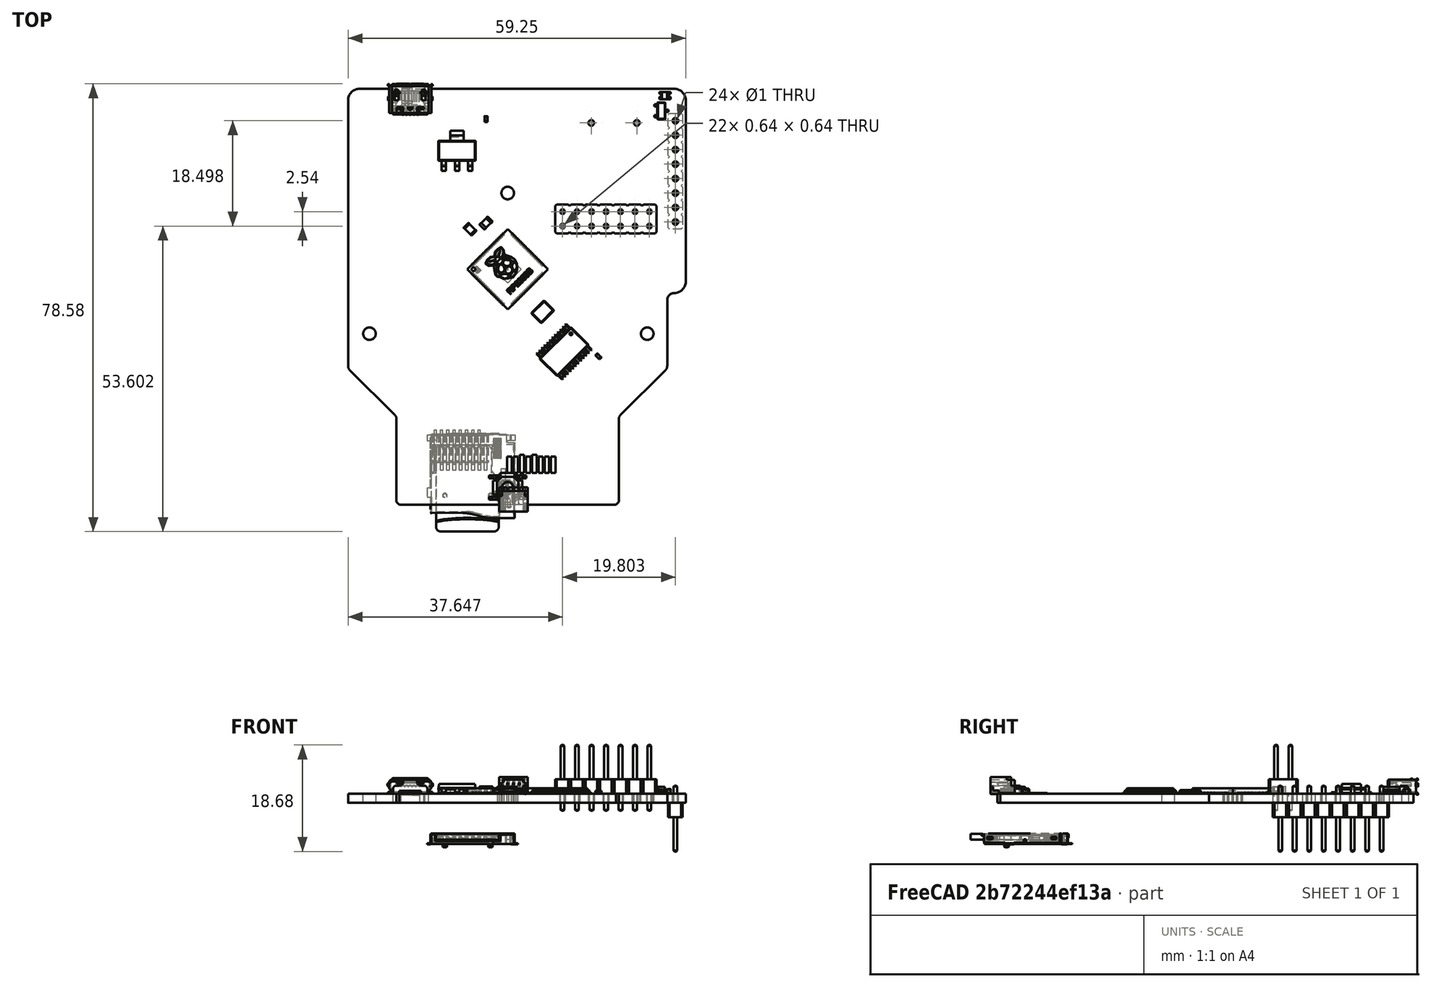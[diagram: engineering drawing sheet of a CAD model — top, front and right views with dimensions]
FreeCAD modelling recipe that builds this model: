
FCSTD DOCUMENT  (FreeCAD 1.0R39285 (Git))
Label: DecentCart2350Board
License: All rights reserved
LicenseURL: http://en.wikipedia.org/wiki/All_rights_reserved
objects: Part::Feature×97, App::Link×62, App::Part×27, PartDesign::CoordinateSystem×1, Sketcher::SketchObject×1
note: 100 computed .brp shape members not serialized (recipe doc carries the construction recipe); baked Part::Feature solids carry a one-line shape summary decoded from their .brp

FEATURE [PartDesign::CoordinateSystem] Local_CS_9dbe
  AttacherType = Attacher::AttachEngine3D
  MapMode = 2
FEATURE [Part::Feature] Pcb_9dbe
  Placement = pos=(-149.761,121.317,0) rot=(0,0,1;0rad)
  shape: bbox 59.25 x 73 x 1.6 mm, 71 faces (baked)
FEATURE [Sketcher::SketchObject] PCB_Sketch_9dbe
  ArcFitTolerance = 1e-06
  FullyConstrained = false
  MakeInternals = false
  sketch-geometry (19):
    g0: LineSegment StartX=19.7929 StartY=12.7071 StartZ=0 EndX=27.7071 EndY=20.6229 EndZ=0
    g1: LineSegment StartX=19.5 StartY=-2.5 StartZ=0 EndX=19.5 EndY=12 EndZ=0
    g2: LineSegment StartX=-26 StartY=70 StartZ=0 EndX=29.25 EndY=70 EndZ=0
    g3: LineSegment StartX=19 StartY=-3 StartZ=0 EndX=19.5 EndY=-2.5 EndZ=0
    g4: LineSegment StartX=28 StartY=32.89 StartZ=0 EndX=28 EndY=21.33 EndZ=0
    g5: LineSegment StartX=19 StartY=-3 StartZ=0 EndX=-19 EndY=-3 EndZ=0
    g6: LineSegment StartX=-28 StartY=21.3171 StartZ=0 EndX=-28 EndY=68 EndZ=0
    g7: LineSegment StartX=31.25 StartY=36.14 StartZ=0 EndX=31.25 EndY=68 EndZ=0
    g8: LineSegment StartX=-19.7929 StartY=12.7071 StartZ=0 EndX=-27.7071 EndY=20.61 EndZ=0
    g9: LineSegment StartX=-19 StartY=-3 StartZ=0 EndX=-19.5 EndY=-2.5 EndZ=0
    g10: LineSegment StartX=-19.5 StartY=-2.5 StartZ=0 EndX=-19.5 EndY=12 EndZ=0
    g11: ArcOfCircle CenterX=-20.5001 CenterY=12 CenterZ=0 NormalX=0 NormalY=0 NormalZ=-1 AngleXU=2.35623 Radius=1.00008 StartAngle=0 EndAngle=0.78533
    g12: ArcOfCircle CenterX=29.25 CenterY=36.14 CenterZ=0 NormalX=0 NormalY=0 NormalZ=-1 AngleXU=3.14159 Radius=2 StartAngle=0 EndAngle=1.5708
    g13: ArcOfCircle CenterX=29.25 CenterY=32.89 CenterZ=0 NormalX=0 NormalY=0 NormalZ=-1 AngleXU=1.30145e-06 Radius=1.25 StartAngle=0 EndAngle=1.57079
    g14: ArcOfCircle CenterX=20.5 CenterY=12 CenterZ=0 NormalX=0 NormalY=0 NormalZ=-1 AngleXU=1.0278e-05 Radius=1.00003 StartAngle=0 EndAngle=0.785377
    g15: ArcOfCircle CenterX=29.25 CenterY=68 CenterZ=0 NormalX=0 NormalY=0 NormalZ=-1 AngleXU=1.5708 Radius=2 StartAngle=0 EndAngle=1.5708
    g16: ArcOfCircle CenterX=-27 CenterY=21.3171 CenterZ=0 NormalX=0 NormalY=0 NormalZ=-1 AngleXU=-0.785398 Radius=0.999999 StartAngle=0 EndAngle=0.785399
    g17: ArcOfCircle CenterX=-26 CenterY=68 CenterZ=0 NormalX=0 NormalY=0 NormalZ=-1 AngleXU=-7.47076e-07 Radius=2 StartAngle=0 EndAngle=1.5708
    g18: ArcOfCircle CenterX=27 CenterY=21.33 CenterZ=0 NormalX=0 NormalY=0 NormalZ=-1 AngleXU=3.14158 Radius=0.999978 StartAngle=0 EndAngle=0.785416
  constraints (19):
    c: Coincident(g6,g16)
    c: Coincident(g6,g17)
    c: Coincident(g8,g16)
    c: Coincident(g2,g17)
    c: Coincident(g8,g11)
    c: Coincident(g9,g10)
    c: Coincident(g10,g11)
    c: Coincident(g5,g9)
    c: Coincident(g3,g5)
    c: Coincident(g1,g3)
    c: Coincident(g1,g14)
    c: Coincident(g0,g14)
    c: Coincident(g0,g18)
    c: Coincident(g4,g18)
    c: Coincident(g4,g13)
    c: Coincident(g12,g13)
    c: Coincident(g2,g15)
    c: Coincident(g7,g12)
    c: Coincident(g7,g15)
FEATURE [App::Part] Board_Geoms_9dbe
  Group = -> [Pcb_9dbe,PCB_Sketch_9dbe]
  Origin = -> Origin
FEATURE [Part::Feature] Shape  label="U6_TSSOP_24_44x78mm_P065mm_249428eb97b7"
  Placement = pos=(9.906,23.836,0) rot=(0,0,-1;0.785398rad)
  shape: bbox 9.765 x 9.765 x 0.97 mm, 396 faces (baked)
FEATURE [Part::Feature] Shape001  label="R30_R_0402_1005Metric_56d1e8ac7ec3"
  Placement = pos=(-3.7846,64.6938,0) rot=(0,0,1;1.5708rad)
  shape: bbox 0.5 x 1 x 0.35 mm, 26 faces (baked)
FEATURE [Part::Feature] Shape002  label="C33_C_0402_1005Metric_439f5c97a156"
  Placement = pos=(15.9258,23.0232,0) rot=(0,0,1;2.35619rad)
  shape: bbox 1.061 x 1.061 x 0.5 mm, 28 faces (baked)
FEATURE [Part::Feature] Shape003  label="U3_RP2350B_5bf34b71a8d2"
  Placement = pos=(0,38.314,0) rot=(0,0,1;0.785398rad)
  shape: bbox 14.16 x 14.16 x 0.9762 mm, 744 faces (baked)
FEATURE [App::Link] C33_C_0402_1005Metric_439f5c97a156_ln_  label="C29_C_0402_1005Metric_d980d0f3218c"
  LinkPlacement = pos=(4.8514,21.55,0) rot=(0,0,1;3.14159rad)
  LinkedObject = -> Shape002
  Placement = pos=(4.8514,21.55,0) rot=(0,0,1;3.14159rad)
FEATURE [App::Link] C33_C_0402_1005Metric_439f5c97a156_ln_001  label="C10_C_0402_1005Metric_251042c45dc4"
  LinkPlacement = pos=(4.9784,42.5812,0) rot=(0,0,1;0.785398rad)
  LinkedObject = -> Shape002
  Placement = pos=(4.9784,42.5812,0) rot=(0,0,1;0.785398rad)
FEATURE [App::Link] R30_R_0402_1005Metric_56d1e8ac7ec3_ln_  label="R10_R_0402_1005Metric_51b1b8e8657a"
  LinkPlacement = pos=(-11.1506,31.4306,0) rot=(0,0,1;3.92699rad)
  LinkedObject = -> Shape001
  Placement = pos=(-11.1506,31.4306,0) rot=(0,0,1;3.92699rad)
FEATURE [App::Link] R30_R_0402_1005Metric_56d1e8ac7ec3_ln_001  label="R24_R_0402_1005Metric_4880820e7255"
  LinkPlacement = pos=(5.7404,41.8338,0) rot=(0,0,1;0.785398rad)
  LinkedObject = -> Shape001
  Placement = pos=(5.7404,41.8338,0) rot=(0,0,1;0.785398rad)
FEATURE [App::Link] C33_C_0402_1005Metric_439f5c97a156_ln_002  label="C39_C_0402_1005Metric_aed9d11787dd"
  LinkPlacement = pos=(21.4376,27.9508,0) rot=(0,0,1;0.785398rad)
  LinkedObject = -> Shape002
  Placement = pos=(21.4376,27.9508,0) rot=(0,0,1;0.785398rad)
FEATURE [App::Link] R30_R_0402_1005Metric_56d1e8ac7ec3_ln_002  label="R7_R_0402_1005Metric_6c02ad4cb323"
  LinkPlacement = pos=(20.32,51.1302,0) rot=(0,0,1;1.5708rad)
  LinkedObject = -> Shape001
  Placement = pos=(20.32,51.1302,0) rot=(0,0,1;1.5708rad)
FEATURE [App::Link] R30_R_0402_1005Metric_56d1e8ac7ec3_ln_003  label="R6_R_0402_1005Metric_24b84eea597d"
  LinkPlacement = pos=(17.4752,51.1302,0) rot=(0,0,1;1.5708rad)
  LinkedObject = -> Shape001
  Placement = pos=(17.4752,51.1302,0) rot=(0,0,1;1.5708rad)
FEATURE [App::Link] C33_C_0402_1005Metric_439f5c97a156_ln_003  label="C24_C_0402_1005Metric_bb1ce9836f4d"
  LinkPlacement = pos=(4.3434,28.9922,0) rot=(0,0,1;2.35619rad)
  LinkedObject = -> Shape002
  Placement = pos=(4.3434,28.9922,0) rot=(0,0,1;2.35619rad)
FEATURE [App::Link] U6_TSSOP_24_44x78mm_P065mm_249428eb97b7_ln_  label="U5_TSSOP_24_44x78mm_P065mm_d589b01f07bd"
  LinkPlacement = pos=(-0.254,19.518,0) rot=(0,0,-1;1.5708rad)
  LinkedObject = -> Shape
  Placement = pos=(-0.254,19.518,0) rot=(0,0,-1;1.5708rad)
FEATURE [Part::Feature] Shape004  label="R28_R_0805_2012Metric_252277e7415b"
  Placement = pos=(-6.604,45.339,0) rot=(0,0,-1;0.785398rad)
  shape: bbox 2.263 x 2.263 x 0.45 mm, 26 faces (baked)
FEATURE [App::Link] R30_R_0402_1005Metric_56d1e8ac7ec3_ln_004  label="R9_R_0402_1005Metric_bd238e743bb6"
  LinkPlacement = pos=(23.1648,51.1302,0) rot=(0,0,1;1.5708rad)
  LinkedObject = -> Shape001
  Placement = pos=(23.1648,51.1302,0) rot=(0,0,1;1.5708rad)
FEATURE [App::Link] C33_C_0402_1005Metric_439f5c97a156_ln_004  label="C16_C_0402_1005Metric_04ddee7b3d28"
  LinkPlacement = pos=(19.3802,51.1556,0) rot=(0,0,1;1.5708rad)
  LinkedObject = -> Shape002
  Placement = pos=(19.3802,51.1556,0) rot=(0,0,1;1.5708rad)
FEATURE [App::Link] C33_C_0402_1005Metric_439f5c97a156_ln_005  label="C25_C_0402_1005Metric_b25ebf576064"
  LinkPlacement = pos=(4.3942,32.1926,0) rot=(0,0,1;0.785398rad)
  LinkedObject = -> Shape002
  Placement = pos=(4.3942,32.1926,0) rot=(0,0,1;0.785398rad)
FEATURE [Part::Feature] Part__Feature  label="TS-1187A v2"
  shape: bbox 5.1 x 5.1 x 1.2 mm, 48 faces (baked)
FEATURE [Part::Feature] Part__Feature001  label="TS-1187A v003"
  shape: bbox 2 x 2 x 1.4 mm, 4 faces (baked)
FEATURE [Part::Feature] Part__Feature002  label="TS-1187A v004"
  shape: bbox 1.15 x 1.15 x 0.7 mm, 10 faces (baked)
FEATURE [Part::Feature] Part__Feature003  label="TS-1187A v005"
  shape: bbox 1.15 x 1.15 x 0.7 mm, 10 faces (baked)
FEATURE [Part::Feature] Part__Feature004  label="TS-1187A v006"
  shape: bbox 1.15 x 1.15 x 0.7 mm, 10 faces (baked)
FEATURE [Part::Feature] Part__Feature005  label="TS-1187A v007"
  shape: bbox 1.15 x 1.15 x 0.7 mm, 10 faces (baked)
FEATURE [Part::Feature] Part__Feature006  label="TS-1187A v008"
  shape: bbox 1.55 x 0.5 x 0.2 mm, 10 faces (baked)
FEATURE [Part::Feature] Part__Feature007  label="TS-1187A v009"
  shape: bbox 1.55 x 0.5 x 0.2 mm, 10 faces (baked)
FEATURE [Part::Feature] Part__Feature008  label="TS-1187A v010"
  shape: bbox 1.55 x 0.5 x 0.2 mm, 10 faces (baked)
FEATURE [Part::Feature] Part__Feature009  label="TS-1187A v011"
  shape: bbox 1.55 x 0.5 x 0.2 mm, 10 faces (baked)
FEATURE [App::Part] TS_1187A_v2  label="SW3_TS-1187A v012_8148cfb37216"
  Group = -> [Part__Feature,Part__Feature001,Part__Feature002,Part__Feature003,Part__Feature004,Part__Feature005,Part__Feature006,Part__Feature007,Part__Feature008,Part__Feature009]
  Origin = -> Origin008
  Placement = pos=(4.5,67.1,0) rot=(0,0,1;3.14159rad)
FEATURE [App::Link] R30_R_0402_1005Metric_56d1e8ac7ec3_ln_005  label="R36_R_0402_1005Metric_a48c821af01a"
  LinkPlacement = pos=(-17.52,43.93,0) rot=(0,0,1;0.785398rad)
  LinkedObject = -> Shape001
  Placement = pos=(-17.52,43.93,0) rot=(0,0,1;0.785398rad)
FEATURE [App::Link] U6_TSSOP_24_44x78mm_P065mm_249428eb97b7_ln_001  label="U1_TSSOP_24_44x78mm_P065mm_cca0021ee69b"
  LinkPlacement = pos=(-16.51,29.932,0) rot=(0,0,1;3.92699rad)
  LinkedObject = -> Shape
  Placement = pos=(-16.51,29.932,0) rot=(0,0,1;3.92699rad)
FEATURE [App::Link] R30_R_0402_1005Metric_56d1e8ac7ec3_ln_006  label="R8_R_0402_1005Metric_3dfb7eb72526"
  LinkPlacement = pos=(22.098,51.1302,0) rot=(0,0,1;1.5708rad)
  LinkedObject = -> Shape001
  Placement = pos=(22.098,51.1302,0) rot=(0,0,1;1.5708rad)
FEATURE [Part::Feature] Part__Feature010  label="Contact009"
  Placement = pos=(-13.13,0,0) rot=(0,0,1;0rad)
  shape: bbox 0.9 x 1.8 x 0.4546 mm, 22 faces (baked)
FEATURE [Part::Feature] Part__Feature011  label="Contact008"
  Placement = pos=(-7.7,0,0) rot=(0,0,1;0rad)
  shape: bbox 0.9 x 6.04 x 0.9096 mm, 26 faces (baked)
FEATURE [Part::Feature] Part__Feature012  label="Contact007"
  Placement = pos=(-6.6,0,0) rot=(0,0,1;0rad)
  shape: bbox 0.9 x 6.04 x 0.9096 mm, 26 faces (baked)
FEATURE [Part::Feature] Part__Feature013  label="Contact006"
  Placement = pos=(-5.5,0,0) rot=(0,0,1;0rad)
  shape: bbox 0.9 x 6.04 x 0.9096 mm, 26 faces (baked)
FEATURE [Part::Feature] Part__Feature014  label="Contact005"
  Placement = pos=(-4.4,0,0) rot=(0,0,1;0rad)
  shape: bbox 0.9 x 6.04 x 0.9096 mm, 26 faces (baked)
FEATURE [Part::Feature] Part__Feature015  label="Contact004"
  Placement = pos=(-3.3,0,0) rot=(0,0,1;0rad)
  shape: bbox 0.9 x 6.04 x 0.9096 mm, 26 faces (baked)
FEATURE [Part::Feature] Part__Feature016  label="Contact003"
  Placement = pos=(-2.2,0,0) rot=(0,0,1;0rad)
  shape: bbox 0.9 x 6.04 x 0.9096 mm, 26 faces (baked)
FEATURE [Part::Feature] Part__Feature017  label="Contact002"
  Placement = pos=(-1.1,0,0) rot=(0,0,1;0rad)
  shape: bbox 0.9 x 6.04 x 0.9096 mm, 26 faces (baked)
FEATURE [App::Part] cont
  Group = -> [Part__Feature010,Part__Feature011,Part__Feature012,Part__Feature013,Part__Feature014,Part__Feature015,Part__Feature016,Part__Feature017]
  Origin = -> Origin009
FEATURE [Part::Feature] Part__Feature018  label="frame002"
  Placement = pos=(0.05,0,-8.83) rot=(0,0,1;0rad)
  shape: bbox 14.8 x 14.69 x 2.22 mm, 238 faces (baked)
FEATURE [Part::Feature] Part__Feature019  label="cover001"
  Placement = pos=(0.3,1.14,-0.54) rot=(0.706791,-0.029864,0.706791;3.07998rad)
  shape: bbox 15.98 x 14.86 x 1.92 mm, 162 faces (baked)
FEATURE [Part::Feature] Part__Feature020  label="spring"
  Placement = pos=(-1.82,8.5,-8.08) rot=(0.15487,0.698575,-0.698575;2.83429rad)
  shape: bbox 1.439 x 3.68 x 1.439 mm, 10 faces (baked)
FEATURE [App::Part] microSD_card_slot  label="J1_microSD_card_slot_e46293b91a5e"
  Group = -> [cont,Part__Feature018,Part__Feature019,Part__Feature020]
  Origin = -> Origin010
  Placement = pos=(11.59,62.758,8.9) rot=(0,0,1;3.14159rad)
FEATURE [Part::Feature] Part__Feature021  label="cont002"
  Placement = pos=(6.9,4,0) rot=(0,0,1;0rad)
  shape: bbox 0.8 x 2.9 x 0.1 mm, 6 faces (baked)
FEATURE [Part::Feature] Part__Feature022  label="cont003"
  Placement = pos=(5.8,4,0) rot=(0,0,1;0rad)
  shape: bbox 0.8 x 2.9 x 0.1 mm, 6 faces (baked)
FEATURE [Part::Feature] Part__Feature023  label="cont005"
  Placement = pos=(3.6,4,0) rot=(0,0,1;0rad)
  shape: bbox 0.8 x 2.9 x 0.1 mm, 6 faces (baked)
FEATURE [Part::Feature] Part__Feature024  label="cont006"
  Placement = pos=(2.5,4.15,0) rot=(0,0,1;0rad)
  shape: bbox 0.8 x 3.2 x 0.1 mm, 6 faces (baked)
FEATURE [Part::Feature] Part__Feature025  label="cont007"
  Placement = pos=(1.4,4,0) rot=(0,0,1;0rad)
  shape: bbox 0.8 x 2.9 x 0.1 mm, 6 faces (baked)
FEATURE [Part::Feature] Part__Feature026  label="cont008"
  Placement = pos=(0.3,4,0) rot=(0,0,1;0rad)
  shape: bbox 0.8 x 2.9 x 0.1 mm, 6 faces (baked)
FEATURE [Part::Feature] Part__Feature027  label="cont001"
  Placement = pos=(8,4,0) rot=(0,0,1;0rad)
  shape: bbox 0.8 x 2.9 x 0.1 mm, 6 faces (baked)
FEATURE [Part::Feature] Part__Feature028  label="cont004"
  Placement = pos=(4.7,4.15,0) rot=(0,0,1;0rad)
  shape: bbox 0.8 x 3.2 x 0.1 mm, 6 faces (baked)
FEATURE [App::Part] contacts
  Group = -> [Part__Feature021,Part__Feature022,Part__Feature023,Part__Feature024,Part__Feature025,Part__Feature026,Part__Feature027,Part__Feature028]
  Origin = -> Origin011
  Placement = pos=(-11.8,0.74,-8.1) rot=(0,0,1;0rad)
FEATURE [Part::Feature] Part__Feature029  label="body"
  Placement = pos=(-7.65,2.35,-8.04) rot=(0,0,1;0rad)
  shape: bbox 11.09 x 15 x 1 mm, 19 faces (baked)
FEATURE [Part::Feature] Part__Feature030  label="microSD001"
  Placement = pos=(-9.65,-4.1,-7.33) rot=(0,0,1;0rad)
  shape: bbox 1.052 x 0.727 x 2e-07 mm, 1 faces, 0 solids (baked)
FEATURE [Part::Feature] Part__Feature031  label="microSD002"
  Placement = pos=(-9.65,-4.1,-7.33) rot=(0,0,1;0rad)
  shape: bbox 0.1517 x 0.7132 x 2e-07 mm, 1 faces, 0 solids (baked)
FEATURE [Part::Feature] Part__Feature032  label="microSD003"
  Placement = pos=(-9.65,-4.1,-7.33) rot=(0,0,1;0rad)
  shape: bbox 0.1704 x 0.168 x 2e-07 mm, 1 faces, 0 solids (baked)
FEATURE [Part::Feature] Part__Feature033  label="microSD004"
  Placement = pos=(-9.65,-4.1,-7.33) rot=(0,0,1;0rad)
  shape: bbox 0.546 x 0.7407 x 2e-07 mm, 1 faces, 0 solids (baked)
FEATURE [Part::Feature] Part__Feature034  label="microSD005"
  Placement = pos=(-9.65,-4.1,-7.33) rot=(0,0,1;0rad)
  shape: bbox 0.4376 x 0.727 x 2e-07 mm, 1 faces, 0 solids (baked)
FEATURE [Part::Feature] Part__Feature035  label="microSD006"
  Placement = pos=(-9.65,-4.1,-7.33) rot=(0,0,1;0rad)
  shape: bbox 0.6757 x 0.7407 x 2e-07 mm, 1 faces, 0 solids (baked)
FEATURE [Part::Feature] Part__Feature036  label="microSD007"
  Placement = pos=(-9.65,-4.1,-7.33) rot=(0,0,1;0rad)
  shape: bbox 0.6041 x 0.972 x 2e-07 mm, 1 faces, 0 solids (baked)
FEATURE [Part::Feature] Part__Feature037  label="microSD008"
  Placement = pos=(-9.65,-4.1,-7.33) rot=(0,0,1;0rad)
  shape: bbox 0.7674 x 0.9445 x 2e-07 mm, 1 faces, 0 solids (baked)
FEATURE [App::Part] microSD009
  Group = -> [Part__Feature030,Part__Feature031,Part__Feature032,Part__Feature033,Part__Feature034,Part__Feature035,Part__Feature036,Part__Feature037]
  Origin = -> Origin012
FEATURE [Part::Feature] Part__Feature038  label="DATA2"
  Placement = pos=(-4.04,1.23,-8.06) rot=(0.707107,0.707107,0;3.14159rad)
  shape: bbox 0.4723 x 0.3582 x 2e-07 mm, 1 faces, 0 solids (baked)
FEATURE [Part::Feature] Part__Feature039  label="DATA003"
  Placement = pos=(-4.04,1.23,-8.06) rot=(0.707107,0.707107,0;3.14159rad)
  shape: bbox 0.4736 x 0.3966 x 2e-07 mm, 1 faces, 0 solids (baked)
FEATURE [Part::Feature] Part__Feature040  label="DATA004"
  Placement = pos=(-4.04,1.23,-8.06) rot=(0.707107,0.707107,0;3.14159rad)
  shape: bbox 0.4723 x 0.3398 x 2e-07 mm, 1 faces, 0 solids (baked)
FEATURE [Part::Feature] Part__Feature041  label="DATA005"
  Placement = pos=(-4.04,1.23,-8.06) rot=(0.707107,0.707107,0;3.14159rad)
  shape: bbox 0.4736 x 0.3966 x 2e-07 mm, 1 faces, 0 solids (baked)
FEATURE [Part::Feature] Part__Feature042  label="DATA006"
  Placement = pos=(-4.04,1.23,-8.06) rot=(0.707107,0.707107,0;3.14159rad)
  shape: bbox 0.4791 x 0.2953 x 2e-07 mm, 1 faces, 0 solids (baked)
FEATURE [App::Part] DATA007
  Group = -> [Part__Feature038,Part__Feature039,Part__Feature040,Part__Feature041,Part__Feature042]
  Origin = -> Origin013
FEATURE [Part::Feature] Part__Feature043  label="DATA3"
  Placement = pos=(-5.14,0.1,-8.06) rot=(0.707107,0.707107,0;3.14159rad)
  shape: bbox 0.4723 x 0.3582 x 2e-07 mm, 1 faces, 0 solids (baked)
FEATURE [Part::Feature] Part__Feature044  label="DATA008"
  Placement = pos=(-5.14,0.1,-8.06) rot=(0.707107,0.707107,0;3.14159rad)
  shape: bbox 0.4736 x 0.3966 x 2e-07 mm, 1 faces, 0 solids (baked)
FEATURE [Part::Feature] Part__Feature045  label="DATA009"
  Placement = pos=(-5.14,0.1,-8.06) rot=(0.707107,0.707107,0;3.14159rad)
  shape: bbox 0.4723 x 0.3398 x 2e-07 mm, 1 faces, 0 solids (baked)
FEATURE [Part::Feature] Part__Feature046  label="DATA010"
  Placement = pos=(-5.14,0.1,-8.06) rot=(0.707107,0.707107,0;3.14159rad)
  shape: bbox 0.4736 x 0.3966 x 2e-07 mm, 1 faces, 0 solids (baked)
FEATURE [Part::Feature] Part__Feature047  label="DATA011"
  Placement = pos=(-5.14,0.1,-8.06) rot=(0.707107,0.707107,0;3.14159rad)
  shape: bbox 0.486 x 0.3001 x 2e-07 mm, 1 faces, 0 solids (baked)
FEATURE [Part::Feature] Part__Feature048  label="DATA012"
  Placement = pos=(-5.14,0.1,-8.06) rot=(0.707107,0.707107,0;3.14159rad)
  shape: bbox 0.4723 x 0.2094 x 2e-07 mm, 1 faces, 0 solids (baked)
FEATURE [Part::Feature] Part__Feature049  label="DATA013"
  Placement = pos=(-5.14,0.1,-8.06) rot=(0.707107,0.707107,0;3.14159rad)
  shape: bbox 0.486 x 0.3482 x 2e-07 mm, 1 faces, 0 solids (baked)
FEATURE [Part::Feature] Part__Feature050  label="DATA014"
  Placement = pos=(-5.14,0.1,-8.06) rot=(0.707107,0.707107,0;3.14159rad)
  shape: bbox 0.4723 x 0.3582 x 2e-07 mm, 1 faces, 0 solids (baked)
FEATURE [App::Part] DATA015
  Group = -> [Part__Feature043,Part__Feature044,Part__Feature045,Part__Feature046,Part__Feature047,Part__Feature048,Part__Feature049,Part__Feature050]
  Origin = -> Origin014
FEATURE [Part::Feature] Part__Feature051  label="CMD"
  Placement = pos=(-6.23,1.68,-8.06) rot=(0.707107,0.707107,0;3.14159rad)
  shape: bbox 0.486 x 0.3482 x 2e-07 mm, 1 faces, 0 solids (baked)
FEATURE [Part::Feature] Part__Feature052  label="CMD001"
  Placement = pos=(-6.23,1.68,-8.06) rot=(0.707107,0.707107,0;3.14159rad)
  shape: bbox 0.4723 x 0.4369 x 2e-07 mm, 1 faces, 0 solids (baked)
FEATURE [Part::Feature] Part__Feature053  label="CMD002"
  Placement = pos=(-6.23,1.68,-8.06) rot=(0.707107,0.707107,0;3.14159rad)
  shape: bbox 0.4723 x 0.3582 x 2e-07 mm, 1 faces, 0 solids (baked)
FEATURE [App::Part] CMD003
  Group = -> [Part__Feature051,Part__Feature052,Part__Feature053]
  Origin = -> Origin015
FEATURE [Part::Feature] Part__Feature054  label="VDD"
  Placement = pos=(-7.32,1.83,-8.06) rot=(0.707107,0.707107,0;3.14159rad)
  shape: bbox 0.4723 x 0.3814 x 2e-07 mm, 1 faces, 0 solids (baked)
FEATURE [Part::Feature] Part__Feature055  label="VDD001"
  Placement = pos=(-7.32,1.83,-8.06) rot=(0.707107,0.707107,0;3.14159rad)
  shape: bbox 0.4723 x 0.3582 x 2e-07 mm, 1 faces, 0 solids (baked)
FEATURE [Part::Feature] Part__Feature056  label="VDD002"
  Placement = pos=(-7.32,1.83,-8.06) rot=(0.707107,0.707107,0;3.14159rad)
  shape: bbox 0.4723 x 0.3582 x 2e-07 mm, 1 faces, 0 solids (baked)
FEATURE [App::Part] VDD003
  Group = -> [Part__Feature054,Part__Feature055,Part__Feature056]
  Origin = -> Origin016
FEATURE [Part::Feature] Part__Feature057  label="CLK"
  Placement = pos=(-8.41,1.93,-8.06) rot=(0.707107,0.707107,0;3.14159rad)
  shape: bbox 0.486 x 0.3482 x 2e-07 mm, 1 faces, 0 solids (baked)
FEATURE [Part::Feature] Part__Feature058  label="CLK001"
  Placement = pos=(-8.41,1.93,-8.06) rot=(0.707107,0.707107,0;3.14159rad)
  shape: bbox 0.4723 x 0.2578 x 2e-07 mm, 1 faces, 0 solids (baked)
FEATURE [Part::Feature] Part__Feature059  label="CLK002"
  Placement = pos=(-8.41,1.93,-8.06) rot=(0.707107,0.707107,0;3.14159rad)
  shape: bbox 0.4723 x 0.3172 x 2e-07 mm, 1 faces, 0 solids (baked)
FEATURE [App::Part] CLK003
  Group = -> [Part__Feature057,Part__Feature058,Part__Feature059]
  Origin = -> Origin017
FEATURE [Part::Feature] Part__Feature060  label="GND"
  Placement = pos=(-9.5,1.68,-8.06) rot=(0.707107,0.707107,0;3.14159rad)
  shape: bbox 0.486 x 0.3847 x 2e-07 mm, 1 faces, 0 solids (baked)
FEATURE [Part::Feature] Part__Feature061  label="GND001"
  Placement = pos=(-9.5,1.68,-8.06) rot=(0.707107,0.707107,0;3.14159rad)
  shape: bbox 0.4723 x 0.343 x 2e-07 mm, 1 faces, 0 solids (baked)
FEATURE [Part::Feature] Part__Feature062  label="GND002"
  Placement = pos=(-9.5,1.68,-8.06) rot=(0.707107,0.707107,0;3.14159rad)
  shape: bbox 0.4723 x 0.3582 x 2e-07 mm, 1 faces, 0 solids (baked)
FEATURE [App::Part] GND003
  Group = -> [Part__Feature060,Part__Feature061,Part__Feature062]
  Origin = -> Origin018
FEATURE [Part::Feature] Part__Feature063  label="DATA0"
  Placement = pos=(-10.65,1.22,-8.06) rot=(0.707107,0.707107,0;3.14159rad)
  shape: bbox 0.4723 x 0.3582 x 2e-07 mm, 1 faces, 0 solids (baked)
FEATURE [Part::Feature] Part__Feature064  label="DATA016"
  Placement = pos=(-10.65,1.22,-8.06) rot=(0.707107,0.707107,0;3.14159rad)
  shape: bbox 0.4736 x 0.3966 x 2e-07 mm, 1 faces, 0 solids (baked)
FEATURE [Part::Feature] Part__Feature065  label="DATA017"
  Placement = pos=(-10.65,1.22,-8.06) rot=(0.707107,0.707107,0;3.14159rad)
  shape: bbox 0.4723 x 0.3398 x 2e-07 mm, 1 faces, 0 solids (baked)
FEATURE [Part::Feature] Part__Feature066  label="DATA018"
  Placement = pos=(-10.65,1.22,-8.06) rot=(0.707107,0.707107,0;3.14159rad)
  shape: bbox 0.4736 x 0.3966 x 2e-07 mm, 1 faces, 0 solids (baked)
FEATURE [Part::Feature] Part__Feature067  label="DATA019"
  Placement = pos=(-10.65,1.22,-8.06) rot=(0.707107,0.707107,0;3.14159rad)
  shape: bbox 0.486 x 0.3033 x 2e-07 mm, 1 faces, 0 solids (baked)
FEATURE [App::Part] DATA020
  Group = -> [Part__Feature063,Part__Feature064,Part__Feature065,Part__Feature066,Part__Feature067]
  Origin = -> Origin019
FEATURE [Part::Feature] Part__Feature068  label="DATA1"
  Placement = pos=(-11.75,1.26,-8.06) rot=(0.707107,0.707107,0;3.14159rad)
  shape: bbox 0.4723 x 0.3582 x 2e-07 mm, 1 faces, 0 solids (baked)
FEATURE [Part::Feature] Part__Feature069  label="DATA021"
  Placement = pos=(-11.75,1.26,-8.06) rot=(0.707107,0.707107,0;3.14159rad)
  shape: bbox 0.4736 x 0.3966 x 2e-07 mm, 1 faces, 0 solids (baked)
FEATURE [Part::Feature] Part__Feature070  label="DATA022"
  Placement = pos=(-11.75,1.26,-8.06) rot=(0.707107,0.707107,0;3.14159rad)
  shape: bbox 0.4723 x 0.3398 x 2e-07 mm, 1 faces, 0 solids (baked)
FEATURE [Part::Feature] Part__Feature071  label="DATA023"
  Placement = pos=(-11.75,1.26,-8.06) rot=(0.707107,0.707107,0;3.14159rad)
  shape: bbox 0.4736 x 0.3966 x 2e-07 mm, 1 faces, 0 solids (baked)
FEATURE [Part::Feature] Part__Feature072  label="DATA024"
  Placement = pos=(-11.75,1.26,-8.06) rot=(0.707107,0.707107,0;3.14159rad)
  shape: bbox 0.4723 x 0.1559 x 2e-07 mm, 1 faces, 0 solids (baked)
FEATURE [App::Part] DATA025
  Group = -> [Part__Feature068,Part__Feature069,Part__Feature070,Part__Feature071,Part__Feature072]
  Origin = -> Origin020
FEATURE [App::Part] sillk
  Group = -> [microSD009,DATA007,DATA015,CMD003,VDD003,CLK003,GND003,DATA020,DATA025]
  Origin = -> Origin021
FEATURE [App::Part] microSD  label="J1_microSD_e46293b91a5e[2]"
  Group = -> [contacts,Part__Feature029,sillk]
  Origin = -> Origin022
  Placement = pos=(11.52,64.008,8.8) rot=(0,0,1;3.14159rad)
FEATURE [App::Link] C33_C_0402_1005Metric_439f5c97a156_ln_006  label="C17_C_0402_1005Metric_c6ca86716594"
  LinkPlacement = pos=(-10.4902,30.7448,0) rot=(0,0,1;3.92699rad)
  LinkedObject = -> Shape002
  Placement = pos=(-10.4902,30.7448,0) rot=(0,0,1;3.92699rad)
FEATURE [App::Link] R30_R_0402_1005Metric_56d1e8ac7ec3_ln_007  label="R3_R_0402_1005Metric_55c9ecff9d97"
  LinkPlacement = pos=(-5.1054,25.36,0) rot=(0,0,1;3.92699rad)
  LinkedObject = -> Shape001
  Placement = pos=(-5.1054,25.36,0) rot=(0,0,1;3.92699rad)
FEATURE [App::Link] C33_C_0402_1005Metric_439f5c97a156_ln_007  label="C19_C_0402_1005Metric_aa6b38768ae2"
  LinkPlacement = pos=(-17.9832,24.5726,0) rot=(0,0,1;0.785398rad)
  LinkedObject = -> Shape002
  Placement = pos=(-17.9832,24.5726,0) rot=(0,0,1;0.785398rad)
FEATURE [App::Link] C33_C_0402_1005Metric_439f5c97a156_ln_008  label="C13_C_0402_1005Metric_ac4835eec644"
  LinkPlacement = pos=(-3.429,32.2688,0) rot=(0,0,1;3.92699rad)
  LinkedObject = -> Shape002
  Placement = pos=(-3.429,32.2688,0) rot=(0,0,1;3.92699rad)
FEATURE [App::Link] C33_C_0402_1005Metric_439f5c97a156_ln_009  label="C2_C_0402_1005Metric_d5aa21b2d2a1"
  LinkPlacement = pos=(-11.2268,17.8162,0) rot=(0,0,1;0.785398rad)
  LinkedObject = -> Shape002
  Placement = pos=(-11.2268,17.8162,0) rot=(0,0,1;0.785398rad)
FEATURE [App::Link] C33_C_0402_1005Metric_439f5c97a156_ln_010  label="C42_C_0402_1005Metric_3308e26e4d18"
  LinkPlacement = pos=(-12.44,51.24,0) rot=(0,0,1;3.92699rad)
  LinkedObject = -> Shape002
  Placement = pos=(-12.44,51.24,0) rot=(0,0,1;3.92699rad)
FEATURE [App::Link] C33_C_0402_1005Metric_439f5c97a156_ln_011  label="C21_C_0402_1005Metric_6886174ada46"
  LinkPlacement = pos=(-2.12,44.7,0) rot=(0,0,1;0.785398rad)
  LinkedObject = -> Shape002
  Placement = pos=(-2.12,44.7,0) rot=(0,0,1;0.785398rad)
FEATURE [App::Link] R30_R_0402_1005Metric_56d1e8ac7ec3_ln_008  label="R4_R_0402_1005Metric_b9c112d264e7"
  LinkPlacement = pos=(15.4432,51.1302,0) rot=(0,0,1;1.5708rad)
  LinkedObject = -> Shape001
  Placement = pos=(15.4432,51.1302,0) rot=(0,0,1;1.5708rad)
FEATURE [App::Link] C33_C_0402_1005Metric_439f5c97a156_ln_012  label="C6_C_0402_1005Metric_b7d84032a39b"
  LinkPlacement = pos=(-4.8768,33.7166,0) rot=(0,0,1;3.92699rad)
  LinkedObject = -> Shape002
  Placement = pos=(-4.8768,33.7166,0) rot=(0,0,1;3.92699rad)
FEATURE [App::Link] C33_C_0402_1005Metric_439f5c97a156_ln_013  label="C12_C_0402_1005Metric_14e4f58a395b"
  LinkPlacement = pos=(3.0734,31.5322,0) rot=(0,0,-1;0.785398rad)
  LinkedObject = -> Shape002
  Placement = pos=(3.0734,31.5322,0) rot=(0,0,-1;0.785398rad)
FEATURE [Part::Feature] Part__Feature073  label="60816e3e-9268-11ed-8af4-a0cec80452fd_part"
  shape: bbox 2.6 x 1.7 x 1 mm, 20 faces (baked)
FEATURE [App::Part] _0816e3e_9268_11ed_8af4_a0cec80452fd  label="60816e3e-9268-11ed-8af4-a0cec80452fd"
  Group = -> [Part__Feature073]
  Origin = -> Origin023
FEATURE [Part::Feature] Part__Feature074  label="6081710e-9268-11ed-8af4-a0cec80452fd_part"
  shape: bbox 0.4598 x 0.9 x 0.16 mm, 6 faces (baked)
FEATURE [Part::Feature] Part__Feature075  label="6081710e-9268-11ed-8af4-a0cec80452fd_part001"
  shape: bbox 0.4598 x 0.9 x 0.16 mm, 6 faces (baked)
FEATURE [App::Part] _081710e_9268_11ed_8af4_a0cec80452fd_part  label="6081710e-9268-11ed-8af4-a0cec80452fd_part002"
  Group = -> [Part__Feature074,Part__Feature075]
  Origin = -> Origin024
FEATURE [App::Part] _081710e_9268_11ed_8af4_a0cec80452fd  label="6081710e-9268-11ed-8af4-a0cec80452fd"
  Group = -> [_081710e_9268_11ed_8af4_a0cec80452fd_part]
  Origin = -> Origin025
FEATURE [Part::Feature] Part__Feature076  label="6081737a-9268-11ed-8af4-a0cec80452fd_part"
  shape: bbox 0.4 x 1.48 x 0.02 mm, 6 faces (baked)
FEATURE [App::Part] _081737a_9268_11ed_8af4_a0cec80452fd  label="6081737a-9268-11ed-8af4-a0cec80452fd"
  Group = -> [Part__Feature076]
  Origin = -> Origin026
FEATURE [App::Part] _081697a_9268_11ed_8af4_a0cec80452fd  label="6081697a-9268-11ed-8af4-a0cec80452fd"
  Group = -> [_0816e3e_9268_11ed_8af4_a0cec80452fd,_081710e_9268_11ed_8af4_a0cec80452fd,_081737a_9268_11ed_8af4_a0cec80452fd]
  Origin = -> Origin027
FEATURE [App::Part] CQ_assembly  label="D1_CQ assembly_46ded2abadd1"
  Group = -> [_081697a_9268_11ed_8af4_a0cec80452fd]
  Origin = -> Origin028
  Placement = pos=(-15,61.23,0) rot=(0,0,1;1.5708rad)
FEATURE [App::Link] C33_C_0402_1005Metric_439f5c97a156_ln_014  label="C27_C_0402_1005Metric_bd2403ac6954"
  LinkPlacement = pos=(-9.75,54.21,0) rot=(0,0,1;3.14159rad)
  LinkedObject = -> Shape002
  Placement = pos=(-9.75,54.21,0) rot=(0,0,1;3.14159rad)
FEATURE [App::Link] R30_R_0402_1005Metric_56d1e8ac7ec3_ln_009  label="R35_R_0402_1005Metric_71611a0bce3b"
  LinkPlacement = pos=(15.1638,35.2914,0) rot=(0,0,1;3.92699rad)
  LinkedObject = -> Shape001
  Placement = pos=(15.1638,35.2914,0) rot=(0,0,1;3.92699rad)
FEATURE [App::Link] C33_C_0402_1005Metric_439f5c97a156_ln_015  label="C9_C_0402_1005Metric_957a496e0a03"
  LinkPlacement = pos=(1.9558,45.5276,0) rot=(0,0,1;0.785398rad)
  LinkedObject = -> Shape002
  Placement = pos=(1.9558,45.5276,0) rot=(0,0,1;0.785398rad)
FEATURE [App::Link] C33_C_0402_1005Metric_439f5c97a156_ln_016  label="C23_C_0402_1005Metric_9e2713827f55"
  LinkPlacement = pos=(18.4262,51.1558,0) rot=(0,0,1;1.5708rad)
  LinkedObject = -> Shape002
  Placement = pos=(18.4262,51.1558,0) rot=(0,0,1;1.5708rad)
FEATURE [App::Link] R30_R_0402_1005Metric_56d1e8ac7ec3_ln_010  label="R5_R_0402_1005Metric_086edd3ead8f"
  LinkPlacement = pos=(16.4592,51.1302,0) rot=(0,0,1;1.5708rad)
  LinkedObject = -> Shape001
  Placement = pos=(16.4592,51.1302,0) rot=(0,0,1;1.5708rad)
FEATURE [App::Link] C33_C_0402_1005Metric_439f5c97a156_ln_017  label="C18_C_0402_1005Metric_165645344e4a"
  LinkPlacement = pos=(-17.3228,23.9122,0) rot=(0,0,1;0.785398rad)
  LinkedObject = -> Shape002
  Placement = pos=(-17.3228,23.9122,0) rot=(0,0,1;0.785398rad)
FEATURE [App::Link] C33_C_0402_1005Metric_439f5c97a156_ln_018  label="C5_C_0402_1005Metric_bc355a2b3d5d"
  LinkPlacement = pos=(5.715,34.2246,0) rot=(0,0,-1;0.785398rad)
  LinkedObject = -> Shape002
  Placement = pos=(5.715,34.2246,0) rot=(0,0,-1;0.785398rad)
FEATURE [App::Link] C33_C_0402_1005Metric_439f5c97a156_ln_019  label="C8_C_0402_1005Metric_b928555f1243"
  LinkPlacement = pos=(-6.1468,41.3366,0) rot=(0,0,1;2.35619rad)
  LinkedObject = -> Shape002
  Placement = pos=(-6.1468,41.3366,0) rot=(0,0,1;2.35619rad)
FEATURE [Part::Feature] Shape005  label="L16_L_0805_2012Metric_0281535a62de"
  Placement = pos=(-3.79,46.43,0) rot=(0,0,1;0.785398rad)
  shape: bbox 2.298 x 2.298 x 1.25 mm, 28 faces (baked)
FEATURE [Part::Feature] Shape006  label="U4_SOT_223_5f523945142b"
  Placement = pos=(-8.89,59.11,0) rot=(0,0,1;1.5708rad)
  shape: bbox 6.5 x 7 x 1.7 mm, 78 faces (baked)
FEATURE [App::Link] C33_C_0402_1005Metric_439f5c97a156_ln_020  label="C31_C_0402_1005Metric_84c232924965"
  LinkPlacement = pos=(2.5146,14.7428,0) rot=(0,0,1;1.5708rad)
  LinkedObject = -> Shape002
  Placement = pos=(2.5146,14.7428,0) rot=(0,0,1;1.5708rad)
FEATURE [Part::Feature] Shape007  label="Q1_SOT_23_9d8ac5fe343f"
  Placement = pos=(26.97,66.12,0) rot=(0,0,1;0rad)
  shape: bbox 2.5 x 3 x 1.2 mm, 76 faces (baked)
FEATURE [App::Link] R30_R_0402_1005Metric_56d1e8ac7ec3_ln_011  label="R34_R_0402_1005Metric_8a8964e957b6"
  LinkPlacement = pos=(29.87,68.3,0) rot=(0,0,1;1.5708rad)
  LinkedObject = -> Shape001
  Placement = pos=(29.87,68.3,0) rot=(0,0,1;1.5708rad)
FEATURE [App::Link] U6_TSSOP_24_44x78mm_P065mm_249428eb97b7_ln_002  label="U2_TSSOP_24_44x78mm_P065mm_d0ac7568970f"
  LinkPlacement = pos=(-10.414,23.836,0) rot=(0,0,1;3.92699rad)
  LinkedObject = -> Shape
  Placement = pos=(-10.414,23.836,0) rot=(0,0,1;3.92699rad)
FEATURE [App::Link] SW3_TS_1187A_v012_8148cfb37216_ln_  label="SW2_TS-1187A v012_394d79c053f1"
  LinkPlacement = pos=(-8.4,67.1,0) rot=(0,0,1;0rad)
  LinkedObject = -> TS_1187A_v2
  Placement = pos=(-8.4,67.1,0) rot=(0,0,1;0rad)
FEATURE [Part::Feature] Part__Feature077  label="SMxB-SRSS-TB"
  shape: bbox 0.2 x 3.7 x 2.45 mm, 30 faces (baked)
FEATURE [Part::Feature] Part__Feature078  label="SMxB-SRSS-TB001"
  shape: bbox 0.2 x 3.7 x 2.45 mm, 30 faces (baked)
FEATURE [Part::Feature] Part__Feature079  label="SMxB-SRSS-TB002"
  shape: bbox 0.2 x 3.7 x 2.45 mm, 30 faces (baked)
FEATURE [Part::Feature] Part__Feature080  label="SMxB-SRSS-TB003"
  shape: bbox 0.2 x 1.5 x 1.25 mm, 11 faces (baked)
FEATURE [Part::Feature] Part__Feature081  label="SMxB-SRSS-TB004"
  shape: bbox 0.2 x 1.5 x 1.25 mm, 11 faces (baked)
FEATURE [Part::Feature] Part__Feature082  label="SMxB-SRSS-TB005"
  shape: bbox 5 x 4.25 x 2.9 mm, 113 faces (baked)
FEATURE [App::Part] SMxB_SRSS_TB  label="J9_SMxB-SRSS-TB006_7e7ccc67e959"
  Group = -> [Part__Feature077,Part__Feature078,Part__Feature079,Part__Feature080,Part__Feature081,Part__Feature082]
  Origin = -> Origin029
  Placement = pos=(12.6332,38.178,0) rot=(0,0,1;3.14159rad)
FEATURE [App::Link] C33_C_0402_1005Metric_439f5c97a156_ln_021  label="C38_C_0402_1005Metric_9d220426103a"
  LinkPlacement = pos=(16.9164,35.5962,0) rot=(0,0,-1;0.785398rad)
  LinkedObject = -> Shape002
  Placement = pos=(16.9164,35.5962,0) rot=(0,0,-1;0.785398rad)
FEATURE [App::Link] C33_C_0402_1005Metric_439f5c97a156_ln_022  label="C34_C_0402_1005Metric_a9f5ada5892b"
  LinkPlacement = pos=(15.2654,22.3628,0) rot=(0,0,1;2.35619rad)
  LinkedObject = -> Shape002
  Placement = pos=(15.2654,22.3628,0) rot=(0,0,1;2.35619rad)
FEATURE [App::Link] R30_R_0402_1005Metric_56d1e8ac7ec3_ln_012  label="R33_R_0402_1005Metric_4fc78a53e28e"
  LinkPlacement = pos=(3.4036,24.344,0) rot=(0,0,-1;1.5708rad)
  LinkedObject = -> Shape001
  Placement = pos=(3.4036,24.344,0) rot=(0,0,-1;1.5708rad)
FEATURE [Part::Feature] Shape008  label="J8_USB_Micro-B_Molex_47346-0001_f12a3e0ad891"
  Placement = pos=(-17.1,67.0975,0) rot=(0,0,1;3.14159rad)
  shape: bbox 7.977 x 5.418 x 2.937 mm, 484 faces (baked)
FEATURE [App::Link] C33_C_0402_1005Metric_439f5c97a156_ln_023  label="C28_C_0402_1005Metric_0eebf704aaba"
  LinkPlacement = pos=(-9.37,64.03,0) rot=(0,0,1;3.14159rad)
  LinkedObject = -> Shape002
  Placement = pos=(-9.37,64.03,0) rot=(0,0,1;3.14159rad)
FEATURE [App::Link] R30_R_0402_1005Metric_56d1e8ac7ec3_ln_013  label="R25_R_0402_1005Metric_619907af2cf0"
  LinkPlacement = pos=(-1.97,48.21,0) rot=(0,0,-1;0.785398rad)
  LinkedObject = -> Shape001
  Placement = pos=(-1.97,48.21,0) rot=(0,0,-1;0.785398rad)
FEATURE [App::Link] R30_R_0402_1005Metric_56d1e8ac7ec3_ln_014  label="R1_R_0402_1005Metric_3510945f31ea"
  LinkPlacement = pos=(2.4612,24.3504,0) rot=(0,0,-1;1.5708rad)
  LinkedObject = -> Shape001
  Placement = pos=(2.4612,24.3504,0) rot=(0,0,-1;1.5708rad)
FEATURE [App::Link] U6_TSSOP_24_44x78mm_P065mm_249428eb97b7_ln_003  label="U8_TSSOP_24_44x78mm_P065mm_4a3d7d93a238"
  LinkPlacement = pos=(16.002,29.932,0) rot=(0,0,-1;0.785398rad)
  LinkedObject = -> Shape
  Placement = pos=(16.002,29.932,0) rot=(0,0,-1;0.785398rad)
FEATURE [App::Link] R30_R_0402_1005Metric_56d1e8ac7ec3_ln_015  label="R2_R_0402_1005Metric_a4cba3dcb5fe"
  LinkPlacement = pos=(8.4328,29.17,0) rot=(0,0,-1;0.785398rad)
  LinkedObject = -> Shape001
  Placement = pos=(8.4328,29.17,0) rot=(0,0,-1;0.785398rad)
FEATURE [App::Link] C33_C_0402_1005Metric_439f5c97a156_ln_024  label="C7_C_0402_1005Metric_66e62140b239"
  LinkPlacement = pos=(-5.1816,42.3164,0) rot=(0,0,1;2.35619rad)
  LinkedObject = -> Shape002
  Placement = pos=(-5.1816,42.3164,0) rot=(0,0,1;2.35619rad)
FEATURE [App::Link] C33_C_0402_1005Metric_439f5c97a156_ln_025  label="C22_C_0402_1005Metric_0f7daab94107"
  LinkPlacement = pos=(-2.78,45.37,0) rot=(0,0,1;0.785398rad)
  LinkedObject = -> Shape002
  Placement = pos=(-2.78,45.37,0) rot=(0,0,1;0.785398rad)
FEATURE [App::Link] C33_C_0402_1005Metric_439f5c97a156_ln_026  label="C40_C_0402_1005Metric_0b39370d082a"
  LinkPlacement = pos=(20.7772,28.6112,0) rot=(0,0,1;0.785398rad)
  LinkedObject = -> Shape002
  Placement = pos=(20.7772,28.6112,0) rot=(0,0,1;0.785398rad)
FEATURE [App::Link] C33_C_0402_1005Metric_439f5c97a156_ln_027  label="C15_C_0402_1005Metric_b01c136d6a1b"
  LinkPlacement = pos=(-6.2738,35.139,0) rot=(0,0,1;3.92699rad)
  LinkedObject = -> Shape002
  Placement = pos=(-6.2738,35.139,0) rot=(0,0,1;3.92699rad)
FEATURE [Part::Feature] Shape009  label="J3_PinHeader_2x07_P254mm_Vertical_93339528d4fb"
  Placement = pos=(24.8866,48.4324,0) rot=(0,0,-1;1.5708rad)
  shape: bbox 17.78 x 5.08 x 11.54 mm, 298 faces (baked)
FEATURE [App::Link] R28_R_0805_2012Metric_252277e7415b_ln_  label="R26_R_0805_2012Metric_359f2953e371"
  LinkPlacement = pos=(-7.9502,43.9928,0) rot=(0,0,-1;0.785398rad)
  LinkedObject = -> Shape004
  Placement = pos=(-7.9502,43.9928,0) rot=(0,0,-1;0.785398rad)
FEATURE [App::Link] R30_R_0402_1005Metric_56d1e8ac7ec3_ln_016  label="R31_R_0402_1005Metric_23446e149bbc"
  LinkPlacement = pos=(5.0476,33.5228,0) rot=(0,0,1;2.35619rad)
  LinkedObject = -> Shape001
  Placement = pos=(5.0476,33.5228,0) rot=(0,0,1;2.35619rad)
FEATURE [App::Link] C33_C_0402_1005Metric_439f5c97a156_ln_028  label="C11_C_0402_1005Metric_c4bec38f26ff"
  LinkPlacement = pos=(6.8834,40.6762,0) rot=(0,0,1;0.785398rad)
  LinkedObject = -> Shape002
  Placement = pos=(6.8834,40.6762,0) rot=(0,0,1;0.785398rad)
FEATURE [App::Link] C33_C_0402_1005Metric_439f5c97a156_ln_029  label="C1_C_0402_1005Metric_80c80a2956ab"
  LinkPlacement = pos=(-4.4196,24.6488,0) rot=(0,0,1;3.92699rad)
  LinkedObject = -> Shape002
  Placement = pos=(-4.4196,24.6488,0) rot=(0,0,1;3.92699rad)
FEATURE [App::Link] C33_C_0402_1005Metric_439f5c97a156_ln_030  label="C3_C_0402_1005Metric_807ef83ce3c4"
  LinkPlacement = pos=(-11.9126,18.502,0) rot=(0,0,1;0.785398rad)
  LinkedObject = -> Shape002
  Placement = pos=(-11.9126,18.502,0) rot=(0,0,1;0.785398rad)
FEATURE [App::Link] C33_C_0402_1005Metric_439f5c97a156_ln_031  label="C26_C_0402_1005Metric_6469debd9077"
  LinkPlacement = pos=(-4.76,55.48,0) rot=(0,0,-1;1.5708rad)
  LinkedObject = -> Shape002
  Placement = pos=(-4.76,55.48,0) rot=(0,0,-1;1.5708rad)
FEATURE [App::Link] C33_C_0402_1005Metric_439f5c97a156_ln_032  label="C32_C_0402_1005Metric_4dd76e80f4a2"
  LinkPlacement = pos=(9.1186,29.8304,0) rot=(0,0,-1;0.785398rad)
  LinkedObject = -> Shape002
  Placement = pos=(9.1186,29.8304,0) rot=(0,0,-1;0.785398rad)
FEATURE [App::Link] Q1_SOT_23_9d8ac5fe343f_ln_  label="Q2_SOT_23_50f1675c441e"
  LinkPlacement = pos=(-15.8863,56.1702,0) rot=(0,0,-1;1.5708rad)
  LinkedObject = -> Shape007
  Placement = pos=(-15.8863,56.1702,0) rot=(0,0,-1;1.5708rad)
FEATURE [App::Link] C33_C_0402_1005Metric_439f5c97a156_ln_033  label="C4_C_0402_1005Metric_8636b596dda0"
  LinkPlacement = pos=(4.318,43.2416,0) rot=(0,0,1;0.785398rad)
  LinkedObject = -> Shape002
  Placement = pos=(4.318,43.2416,0) rot=(0,0,1;0.785398rad)
FEATURE [App::Link] R30_R_0402_1005Metric_56d1e8ac7ec3_ln_017  label="R32_R_0402_1005Metric_82362ff6eb54"
  LinkPlacement = pos=(8.001,55.9562,0) rot=(0,0,1;1.5708rad)
  LinkedObject = -> Shape001
  Placement = pos=(8.001,55.9562,0) rot=(0,0,1;1.5708rad)
FEATURE [Part::Feature] Shape010  label="X1_Crystal_SMD_Abracon_ABM8G-4Pin_3.2x2.5mm_7d0c7747cc04"
  Placement = pos=(6.1468,30.8464,0) rot=(0,0,1;0.785398rad)
  shape: bbox 3.889 x 3.891 x 0.64 mm, 28 faces (baked)
FEATURE [Part::Feature] Shape011  label="D2_D_0805_9f8cde1107a4"
  Placement = pos=(27.62,68.82,0) rot=(0,0,1;3.14159rad)
  shape: bbox 2 x 1.27 x 0.8 mm, 39 faces (baked)
FEATURE [App::Link] C33_C_0402_1005Metric_439f5c97a156_ln_034  label="C20_C_0402_1005Metric_31c811988362"
  LinkPlacement = pos=(-0.64,46.88,0) rot=(0,0,-1;0.785398rad)
  LinkedObject = -> Shape002
  Placement = pos=(-0.64,46.88,0) rot=(0,0,-1;0.785398rad)
FEATURE [App::Link] C33_C_0402_1005Metric_439f5c97a156_ln_035  label="C14_C_0402_1005Metric_99a20b7e1a14"
  LinkPlacement = pos=(3.7084,32.8784,0) rot=(0,0,1;3.92699rad)
  LinkedObject = -> Shape002
  Placement = pos=(3.7084,32.8784,0) rot=(0,0,1;3.92699rad)
FEATURE [App::Link] C33_C_0402_1005Metric_439f5c97a156_ln_036  label="C30_C_0402_1005Metric_526f7df735bc"
  LinkPlacement = pos=(3.429,14.7428,0) rot=(0,0,1;1.5708rad)
  LinkedObject = -> Shape002
  Placement = pos=(3.429,14.7428,0) rot=(0,0,1;1.5708rad)
FEATURE [App::Part] Top_9dbe
  Group = -> [Shape,Shape001,Shape002,Shape003,C33_C_0402_1005Metric_439f5c97a156_ln_,C33_C_0402_1005Metric_439f5c97a156_ln_001,R30_R_0402_1005Metric_56d1e8ac7ec3_ln_,R30_R_0402_1005Metric_56d1e8ac7ec3_ln_001,C33_C_0402_1005Metric_439f5c97a156_ln_002,R30_R_0402_1005Metric_56d1e8ac7ec3_ln_002,R30_R_0402_1005Metric_56d1e8ac7ec3_ln_003,C33_C_0402_1005Metric_439f5c97a156_ln_003,+67 more]
  Origin = -> Origin003
FEATURE [Part::Feature] Shape012  label="J7_PinHeader_1x08_P254mm_Vertical_c7cf26157386"
  Placement = pos=(29.45,46.61,-1.6) rot=(1,0,0;3.14159rad)
  shape: bbox 2.54 x 20.32 x 11.54 mm, 196 faces (baked)
FEATURE [App::Part] Bot_9dbe
  Group = -> [Shape012]
  Origin = -> Origin004
FEATURE [App::Part] Step_Models_9dbe
  Group = -> [Top_9dbe,Bot_9dbe]
  Origin = -> Origin002
FEATURE [App::Part] Board_9dbe  label="DecentCart"
  Group = -> [Local_CS_9dbe,Board_Geoms_9dbe,Step_Models_9dbe]
  Origin = -> Origin001
